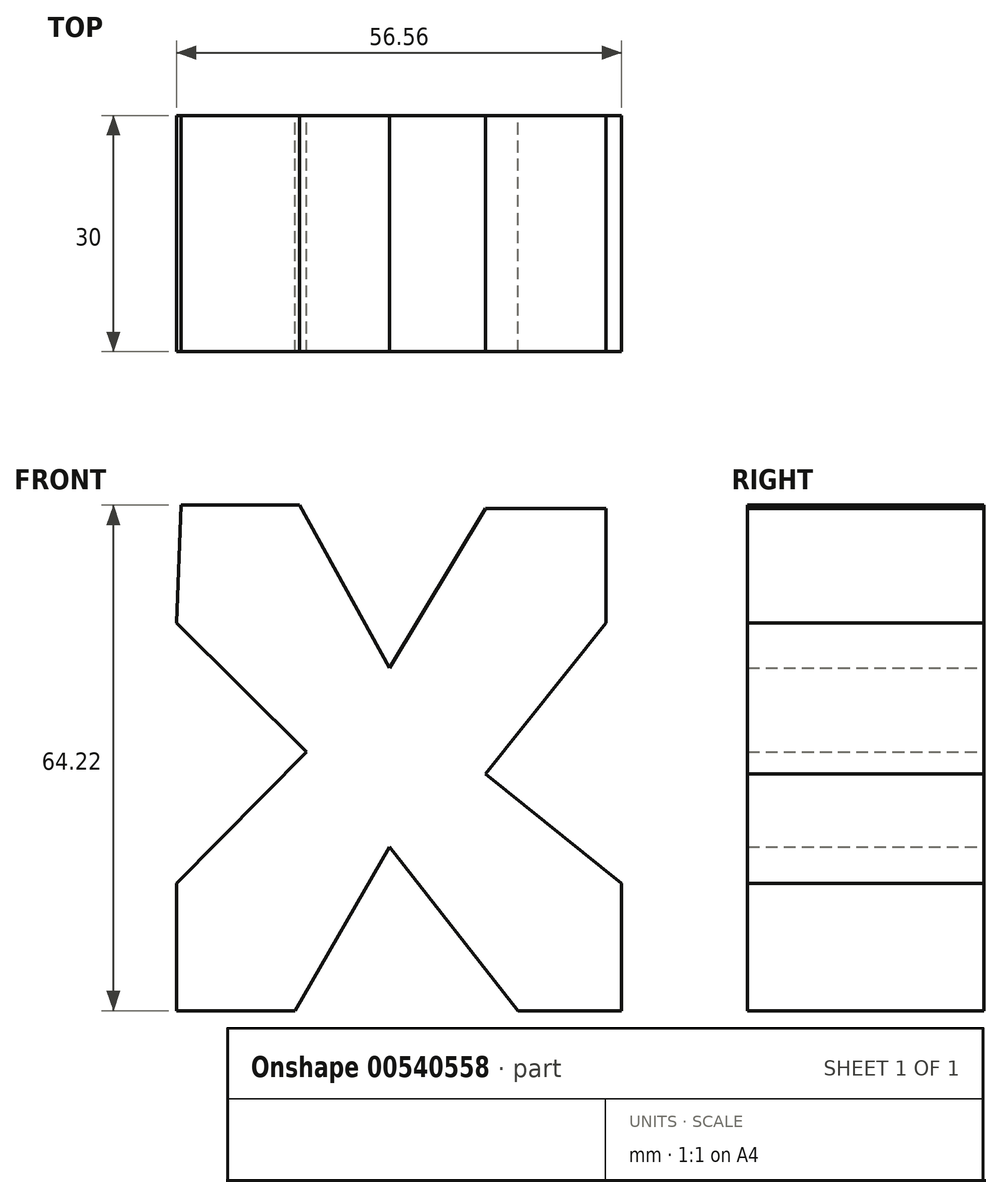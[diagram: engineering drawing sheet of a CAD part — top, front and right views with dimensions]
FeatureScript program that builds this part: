
annotation { "Feature Type Name" : "Feature", "Feature Type Description" : "" }
export const myFeature = defineFeature(function(context is Context, id is Id, definition is map)
    precondition{}
    {
        {
            var Q0;
            Q0=qCreatedBy(makeId("Front.planeOp"),FACE);
            var sketch = newSketch(context, id + "F0", { "sketchPlane" : qUnion([Q0])});
            skLineSegment(sketch, "E0", {"start": v(-65.79, -45.28) * mm, "end": v(-50.79, -45.28) * mm});
            skLineSegment(sketch, "E1", {"start": v(-50.79, -45.28) * mm, "end": v(-38.79, -24.5) * mm});
            skLineSegment(sketch, "E2", {"start": v(-38.79, -24.5) * mm, "end": v(-22.48, -45.28) * mm});
            skLineSegment(sketch, "E3", {"start": v(-22.48, -45.28) * mm, "end": v(-9.28, -45.28) * mm});
            skLineSegment(sketch, "E4", {"start": v(-9.28, -45.28) * mm, "end": v(-9.28, -29.08) * mm});
            skLineSegment(sketch, "E5", {"start": v(-9.28, -29.08) * mm, "end": v(-26.6, -15.2) * mm});
            skLineSegment(sketch, "E6", {"start": v(-26.6, -15.2) * mm, "end": v(-11.26, 3.95) * mm});
            skLineSegment(sketch, "E7", {"start": v(-11.26, 3.95) * mm, "end": v(-11.26, 18.53) * mm});
            skLineSegment(sketch, "E8", {"start": v(-11.26, 18.53) * mm, "end": v(-26.6, 18.53) * mm});
            skLineSegment(sketch, "E9", {"start": v(-26.6, 18.53) * mm, "end": v(-38.79, -1.76) * mm});
            skLineSegment(sketch, "E10", {"start": v(-65.84, 3.95) * mm, "end": v(-49.3, -12.39) * mm});
            skLineSegment(sketch, "E11", {"start": v(-49.3, -12.39) * mm, "end": v(-65.79, -29.08) * mm});
            skLineSegment(sketch, "E12", {"start": v(-65.79, -29.08) * mm, "end": v(-65.79, -45.28) * mm});
            skPoint(sketch, "E13.start.orphan", {"position": v(-50.79, 16.22) * mm});
            skLineSegment(sketch, "E14", {"start": v(-38.79, -1.76) * mm, "end": v(-50.22, 18.94) * mm});
            skLineSegment(sketch, "E15", {"start": v(-50.22, 18.94) * mm, "end": v(-65.22, 18.94) * mm});
            skLineSegment(sketch, "E16", {"start": v(-65.22, 18.94) * mm, "end": v(-65.84, 3.95) * mm});
            skSolve(sketch);
        }
        {
            var Q0;
            Q0 = qSketchRegion(id + "F0", true);
            extrude(context, id + "F1", {"entities" : qUnion([Q0]), "depth" : 30 * mm, "offsetDistance" : 25 * mm});
        }
    });
